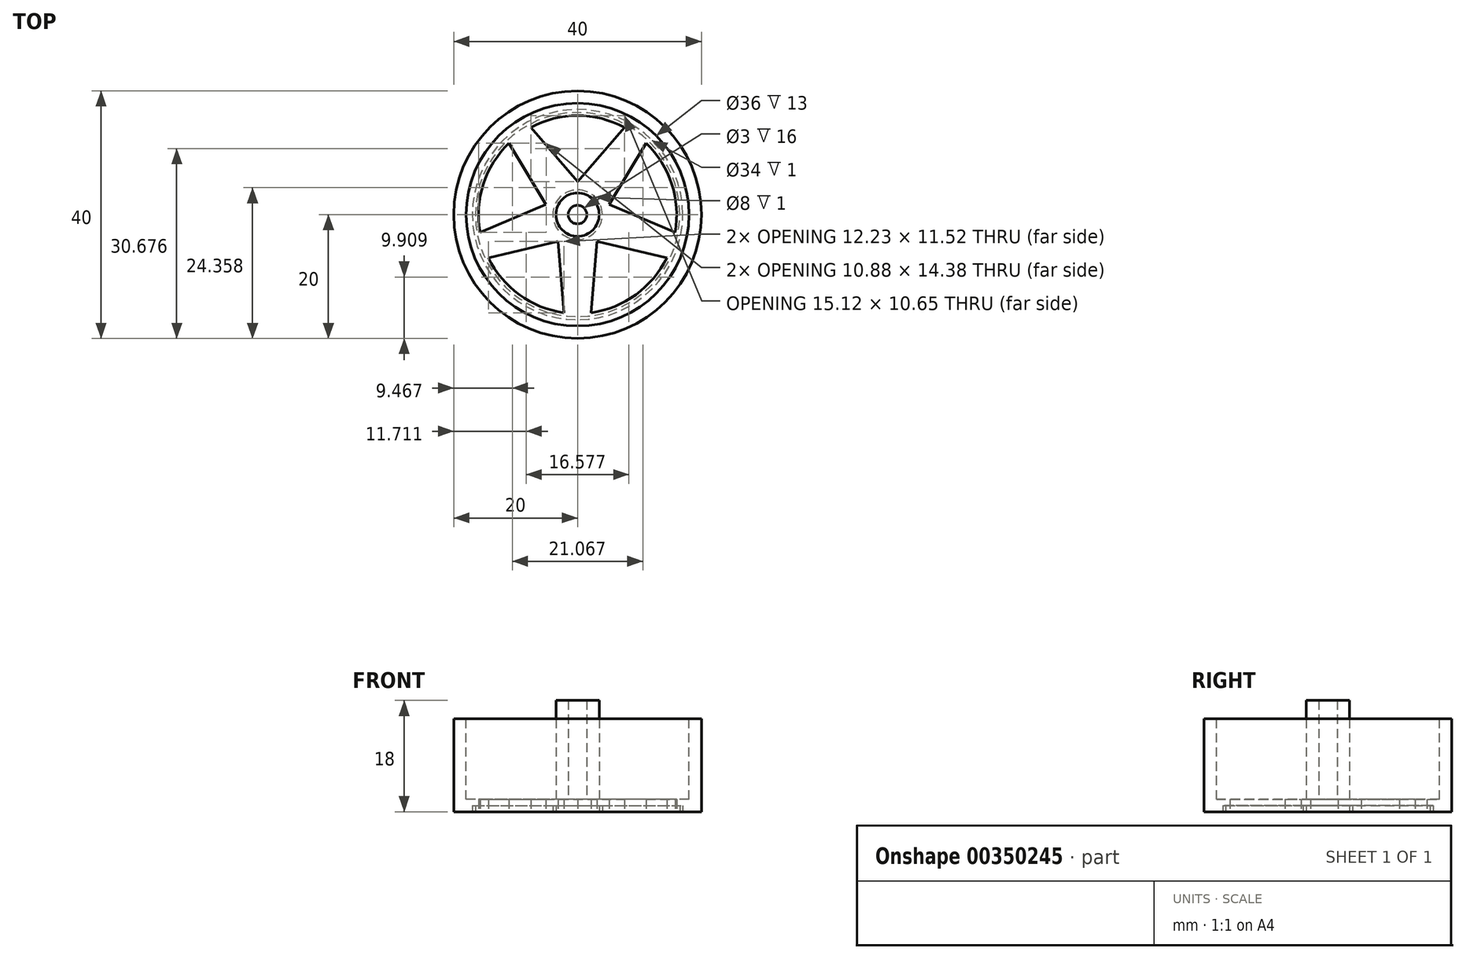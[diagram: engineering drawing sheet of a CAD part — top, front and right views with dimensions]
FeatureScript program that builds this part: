
annotation { "Feature Type Name" : "Feature", "Feature Type Description" : "" }
export const myFeature = defineFeature(function(context is Context, id is Id, definition is map)
    precondition{}
    {
        {
            var Q0;
            Q0=qCreatedBy(makeId("Top.planeOp"),FACE);
            var sketch = newSketch(context, id + "F0", { "sketchPlane" : qUnion([Q0])});
            skCircle(sketch, "E0", {"center": v(0, 0) * mm, "radius": 20 * mm});
            skSolve(sketch);
        }
        {
            var Q0;
            Q0=makeQuery(id+"F0.imprint","IMPRINT",FACE,{"disambiguationData":[TD([[makeQuery(id+"F0.imprint","IMPRINT",EDGE,{"derivedFrom":sQuery(id+"F0.wireOp",EDGE,"E0")}),1.0]])]});
            extrude(context, id + "F1", {"entities" : qUnion([Q0]), "depth" : 15 * mm, "offsetDistance" : 25 * mm});
        }
        {
            var Q0;
            Q0=makeQuery(id+"F1.opExtrude","CAP_FACE",FACE,{"disambiguationData":[OSD([sQuery(id+"F0.wireOp",EDGE,"E0")])],"isStart":false});
            var sketch = newSketch(context, id + "F2", { "sketchPlane" : qUnion([Q0])});
            skCircle(sketch, "E1", {"center": v(0, 0) * mm, "radius": 18 * mm});
            skSolve(sketch);
        }
        {
            var Q0;
            Q0=makeQuery(id+"F2.imprint","IMPRINT",FACE,{"disambiguationData":[TD([[makeQuery(id+"F2.imprint","IMPRINT",EDGE,{"derivedFrom":sQuery(id+"F2.wireOp",EDGE,"E1")}),1.0]])]});
            extrude(context, id + "F3", {"entities" : qUnion([Q0]), "operationType" : NewBodyOperationType.REMOVE, "oppositeDirection" : true, "depth" : 13 * mm, "offsetDistance" : 25 * mm});
        }
        {
            var Q0;
            Q0=makeQuery(id+"F3.boolean.opBoolean","COPY",FACE,{"derivedFrom":makeQuery(id+"F3.opExtrude","CAP_FACE",FACE,{"disambiguationData":[OSD([sQuery(id+"F2.wireOp",EDGE,"E1")])],"isStart":false})});
            var sketch = newSketch(context, id + "F4", { "sketchPlane" : qUnion([Q0])});
            skCircle(sketch, "E2", {"center": v(0, 0) * mm, "radius": 1.5 * mm});
            skCircle(sketch, "E3", {"center": v(0, 0) * mm, "radius": 3.5 * mm});
            skSolve(sketch);
        }
        {
            var Q0;
            Q0=makeQuery(id+"F1.opExtrude","CAP_FACE",FACE,{"disambiguationData":[OSD([sQuery(id+"F0.wireOp",EDGE,"E0")])],"isStart":true});
            var sketch = newSketch(context, id + "F5", { "sketchPlane" : qUnion([Q0])});
            skLineSegment(sketch, "E4", {"start": v(0, 0) * mm, "end": v(2, 0) * mm});
            skLineSegment(sketch, "E5", {"start": v(2.17, 15.85) * mm, "end": v(3.15, 4.33) * mm});
            skLineSegment(sketch, "E6.MirrorCS", {"start": v(-2.17, 15.85) * mm, "end": v(-3.15, 4.33) * mm});
            skLineSegment(sketch, "E7.1.0", {"start": v(-15.75, 2.83) * mm, "end": v(-5.1, -1.65) * mm});
            skLineSegment(sketch, "E7.1.4", {"start": v(-14.4, 6.96) * mm, "end": v(-3.15, 4.33) * mm});
            skLineSegment(sketch, "E7.2.0", {"start": v(-7.56, -14.1) * mm, "end": v(0, -5.35) * mm});
            skLineSegment(sketch, "E7.2.4", {"start": v(-11.07, -11.55) * mm, "end": v(-5.1, -1.65) * mm});
            skLineSegment(sketch, "E7.3.0", {"start": v(11.07, -11.55) * mm, "end": v(5.1, -1.65) * mm});
            skLineSegment(sketch, "E7.3.4", {"start": v(7.56, -14.1) * mm, "end": v(0, -5.35) * mm});
            skLineSegment(sketch, "E7.4.0", {"start": v(14.4, 6.96) * mm, "end": v(3.15, 4.33) * mm});
            skLineSegment(sketch, "E7.4.4", {"start": v(15.75, 2.83) * mm, "end": v(5.1, -1.65) * mm});
            skPoint(sketch, "E7.center", {"position": v(0, 0) * mm});
            skArc(sketch, "E8", {"start": v(-2.17, 15.85) * mm, "mid": v(-9.4, 12.94) * mm, "end": v(-14.4, 6.96) * mm});
            skPoint(sketch, "E9.orphan", {"position": v(-2, 17.89) * mm});
            skPoint(sketch, "E10.trimOffspring.end.orphan", {"position": v(2, 17.89) * mm});
            skPoint(sketch, "E11.orphan", {"position": v(16.4, 7.43) * mm});
            skPoint(sketch, "E12.orphan", {"position": v(17.63, 3.63) * mm});
            skPoint(sketch, "E13.orphan", {"position": v(12.13, -13.3) * mm});
            skPoint(sketch, "E14.orphan", {"position": v(-8.9, -15.65) * mm});
            skPoint(sketch, "E15.orphan", {"position": v(-17.63, 3.63) * mm});
            skPoint(sketch, "E16.orphan", {"position": v(-16.4, 7.43) * mm});
            skCircle(sketch, "E17", {"center": v(0, 0) * mm, "radius": 16.5 * mm});
            skCircle(sketch, "E18", {"center": v(0, 0) * mm, "radius": 17 * mm});
            skArc(sketch, "E19.trimOffspring", {"start": v(14.4, 6.96) * mm, "mid": v(9.4, 12.94) * mm, "end": v(2.17, 15.85) * mm});
            skArc(sketch, "E20.trimOffspring", {"start": v(11.07, -11.55) * mm, "mid": v(15.22, -4.94) * mm, "end": v(15.75, 2.83) * mm});
            skArc(sketch, "E21.trimOffspring", {"start": v(-7.56, -14.1) * mm, "mid": v(0, -16) * mm, "end": v(7.56, -14.1) * mm});
            skArc(sketch, "E22.trimOffspring", {"start": v(-15.75, 2.83) * mm, "mid": v(-15.22, -4.94) * mm, "end": v(-11.07, -11.55) * mm});
            skSolve(sketch);
        }
        {
            var Q0;
            Q0=makeQuery(id+"F4.imprint","IMPRINT",FACE,{"disambiguationData":[TD([[makeQuery(id+"F4.imprint","IMPRINT",EDGE,{"derivedFrom":sQuery(id+"F4.wireOp",EDGE,"E2")}),-1.0]])]});
            extrude(context, id + "F6", {"entities" : qUnion([Q0]), "operationType" : NewBodyOperationType.ADD, "depth" : 16 * mm, "offsetDistance" : 25 * mm});
        }
        {
            var Q0;
            Q0=makeQuery(id+"F5.imprint","IMPRINT",FACE,{"disambiguationData":[TD([[makeQuery(id+"F5.imprint","IMPRINT",EDGE,{"derivedFrom":sQuery(id+"F5.wireOp",EDGE,"E7.2.0")}),-1.0]])]});
            var Q1;
            Q1=makeQuery(id+"F5.imprint","IMPRINT",FACE,{"disambiguationData":[TD([[makeQuery(id+"F5.imprint","IMPRINT",EDGE,{"derivedFrom":sQuery(id+"F5.wireOp",EDGE,"E7.1.0")}),-1.0]])]});
            var Q2;
            Q2=makeQuery(id+"F5.imprint","IMPRINT",FACE,{"disambiguationData":[TD([[makeQuery(id+"F5.imprint","IMPRINT",EDGE,{"derivedFrom":sQuery(id+"F5.wireOp",EDGE,"E6.MirrorCS")}),-1.0]])]});
            var Q3;
            Q3=makeQuery(id+"F5.imprint","IMPRINT",FACE,{"disambiguationData":[TD([[makeQuery(id+"F5.imprint","IMPRINT",EDGE,{"derivedFrom":sQuery(id+"F5.wireOp",EDGE,"E5")}),1.0]])]});
            var Q4;
            Q4=makeQuery(id+"F5.imprint","IMPRINT",FACE,{"disambiguationData":[TD([[makeQuery(id+"F5.imprint","IMPRINT",EDGE,{"derivedFrom":sQuery(id+"F5.wireOp",EDGE,"E7.3.0")}),-1.0]])]});
            extrude(context, id + "F7", {"entities" : qUnion([Q0, Q1, Q2, Q3, Q4]), "operationType" : NewBodyOperationType.REMOVE, "oppositeDirection" : true, "depth" : 2 * mm});
        }
        {
            var Q0;
            Q0 = qSketchRegion(id + "F5", true);
            extrude(context, id + "F8", {"entities" : qUnion([Q0]), "operationType" : NewBodyOperationType.REMOVE, "oppositeDirection" : true, "depth" : 1 * mm});
        }
        {
            var Q0;
            Q0=makeQuery(id+"F8.boolean.opBoolean","SPLIT",FACE,{"disambiguationData":[TD([makeQuery(id+"F7.boolean.opBoolean","COPY",FACE,{"derivedFrom":makeQuery(id+"F7.opExtrude","SWEPT_FACE",FACE,{"disambiguationData":[OSD([sQuery(id+"F5.wireOp",EDGE,"E5")])]})})])],"derivedFrom":makeQuery(id+"F1.opExtrude","CAP_FACE",FACE,{"disambiguationData":[OSD([sQuery(id+"F0.wireOp",EDGE,"E0")])],"isStart":true})});
            var sketch = newSketch(context, id + "F9", { "sketchPlane" : qUnion([Q0])});
            skCircle(sketch, "E23", {"center": v(0, 0) * mm, "radius": 3.5 * mm});
            skCircle(sketch, "E24", {"center": v(0, 0) * mm, "radius": 4 * mm});
            skSolve(sketch);
        }
        {
            var Q0;
            Q0=makeQuery(id+"F9.imprint","IMPRINT",FACE,{"disambiguationData":[TD([[makeQuery(id+"F9.imprint","IMPRINT",EDGE,{"derivedFrom":sQuery(id+"F9.wireOp",EDGE,"E23")}),-1.0]])]});
            extrude(context, id + "F10", {"entities" : qUnion([Q0]), "operationType" : NewBodyOperationType.REMOVE, "oppositeDirection" : true, "depth" : 1 * mm});
        }
    });
